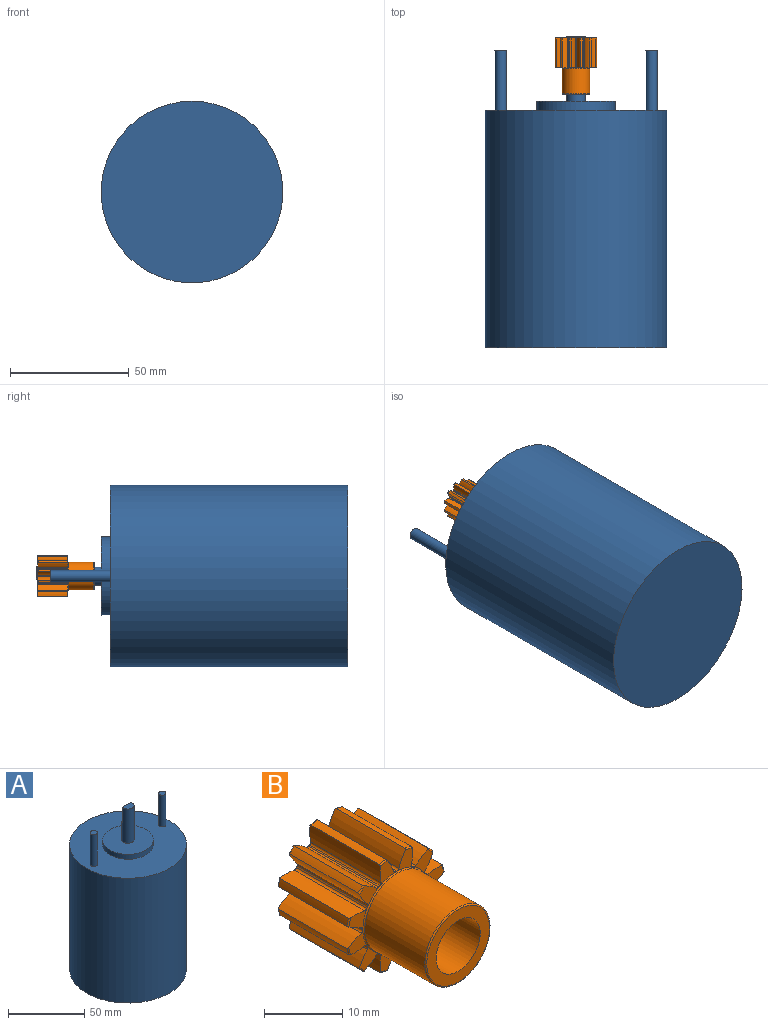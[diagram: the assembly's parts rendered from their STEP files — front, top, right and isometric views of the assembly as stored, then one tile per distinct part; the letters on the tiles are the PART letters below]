
ASSEMBLY  parts=2 mates=1
PART A: 13 faces, bbox 76.5x76.5x131.3 mm
  f0: cylinder r=38.25mm len=100mm, axis (0,0,-1), area 24033.2mm2, adj f1,f2
  f1: plane 76.5x76.5mm, normal (0,0,1), area 3696.7mm2, adj f0,f3,f9,f11
  f2: plane 76.5x76.5mm, normal (0,0,-1), area 4596.3mm2, adj f0
  f3: cylinder r=16.57mm len=33.15mm, axis (0,0,-1), area 402mm2, adj f1,f4
  f4: plane 33.15x33.15mm, normal (0,0,1), area 813.6mm2, adj f3,f5
  f5: cylinder r=3.97mm len=27.45mm, axis (0,0,-1), area 559mm2, adj f4,f6,f7,f8
  f6: plane 7.94x5.24mm, normal (0,0,1), area 34.6mm2, adj f5,f7
  f7: plane 12.7x7.52mm, normal (0,1,0), area 95.5mm2, adj f5,f6,f8
  f8: plane 7.52x2.7mm, normal (0,0,1), area 14.8mm2, adj f5,f7
  f9: cylinder r=2.41mm len=25.4mm, axis (0,0,-1), area 385.1mm2, adj f1,f10
  f10: plane 4.83x4.83mm, normal (0,0,1), area 18.3mm2, adj f9
  f11: cylinder r=2.41mm len=25.4mm, axis (0,0,-1), area 385.1mm2, adj f1,f12
  f12: plane 4.83x4.83mm, normal (0,0,1), area 18.3mm2, adj f11
PART B: 103 faces, bbox 17.5x23.9x17.5 mm
  f0: cylinder r=8.89mm len=12.34mm, axis (0,1,0), area 14.2mm2, adj f1,f2,f94,f98
  f1: torus R=8.71mm, axis (0,-1,0), area 0.3mm2, adj f0,f36,f94,f98
  f2: torus R=8.71mm, axis (0,1,0), area 0.3mm2, adj f0,f38,f94,f98
  f3: cylinder r=8.89mm len=12.34mm, axis (0,1,0), area 14.2mm2, adj f4,f5,f89,f93
  f4: torus R=8.71mm, axis (0,-1,0), area 0.3mm2, adj f3,f36,f89,f93
  f5: torus R=8.71mm, axis (0,1,0), area 0.3mm2, adj f3,f38,f89,f93
  f6: cylinder r=8.89mm len=12.34mm, axis (0,1,0), area 14.2mm2, adj f7,f8,f84,f88
  f7: torus R=8.71mm, axis (0,-1,0), area 0.3mm2, adj f6,f36,f84,f88
  f8: torus R=8.71mm, axis (0,1,0), area 0.3mm2, adj f6,f38,f84,f88
  f9: cylinder r=8.89mm len=12.34mm, axis (0,1,0), area 14.2mm2, adj f10,f11,f79,f83
  f10: torus R=8.71mm, axis (0,-1,0), area 0.3mm2, adj f9,f36,f79,f83
  f11: torus R=8.71mm, axis (0,1,0), area 0.3mm2, adj f9,f38,f79,f83
  f12: cylinder r=8.89mm len=12.34mm, axis (0,1,0), area 14.2mm2, adj f13,f14,f74,f78
  f13: torus R=8.71mm, axis (0,-1,0), area 0.3mm2, adj f12,f36,f74,f78
  f14: torus R=8.71mm, axis (0,1,0), area 0.3mm2, adj f12,f38,f74,f78
  f15: cylinder r=8.89mm len=12.34mm, axis (0,1,0), area 14.2mm2, adj f16,f17,f69,f73
  f16: torus R=8.71mm, axis (0,-1,0), area 0.3mm2, adj f15,f36,f69,f73
  f17: torus R=8.71mm, axis (0,1,0), area 0.3mm2, adj f15,f38,f69,f73
  f18: cylinder r=8.89mm len=12.34mm, axis (0,1,0), area 14.2mm2, adj f19,f20,f64,f68
  f19: torus R=8.71mm, axis (0,-1,0), area 0.3mm2, adj f18,f36,f64,f68
  f20: torus R=8.71mm, axis (0,1,0), area 0.3mm2, adj f18,f38,f64,f68
  f21: cylinder r=8.89mm len=12.34mm, axis (0,1,0), area 14.2mm2, adj f22,f23,f59,f63
  f22: torus R=8.71mm, axis (0,-1,0), area 0.3mm2, adj f21,f36,f59,f63
  f23: torus R=8.71mm, axis (0,1,0), area 0.3mm2, adj f21,f38,f59,f63
  f24: cylinder r=8.89mm len=12.34mm, axis (0,1,0), area 14.2mm2, adj f25,f26,f54,f58
  f25: torus R=8.71mm, axis (0,-1,0), area 0.3mm2, adj f24,f36,f54,f58
  f26: torus R=8.71mm, axis (0,1,0), area 0.3mm2, adj f24,f38,f54,f58
  f27: cylinder r=8.89mm len=12.34mm, axis (0,1,0), area 14.2mm2, adj f28,f29,f49,f53
  f28: torus R=8.71mm, axis (0,-1,0), area 0.3mm2, adj f27,f36,f49,f53
  f29: torus R=8.71mm, axis (0,1,0), area 0.3mm2, adj f27,f38,f49,f53
  f30: cylinder r=8.89mm len=12.34mm, axis (0,1,0), area 14.2mm2, adj f31,f32,f44,f48
  f31: torus R=8.71mm, axis (0,-1,0), area 0.3mm2, adj f30,f36,f44,f48
  f32: torus R=8.71mm, axis (0,1,0), area 0.3mm2, adj f30,f38,f44,f48
  f33: cylinder r=3.97mm len=23.88mm, axis (0,1,0), area 595.4mm2, adj f34,f38
  f34: plane 11.33x11.33mm, normal (0,-1,0), area 51.3mm2, adj f33,f39
  f35: cylinder r=5.84mm len=11.68mm, axis (0,1,0), area 397.2mm2, adj f39,f40
  f36: plane 17.12x17.12mm, normal (0,-1,0), area 65.6mm2, adj f1,f4,f7,f10,f13,f16,f19,f22
  f37: cylinder r=8.89mm len=12.34mm, axis (0,1,0), area 14.2mm2, adj f41,f42,f43,f99
  f38: plane 17.12x17.12mm, normal (0,1,0), area 129.9mm2, adj f2,f5,f8,f11,f14,f17,f20,f23
  f39: torus R=5.66mm, axis (0,-1,0), area 10.1mm2, adj f34,f35
  f40: torus R=6.02mm, axis (0,-1,0), area 10.4mm2, adj f35,f36
  f41: torus R=8.71mm, axis (0,-1,0), area 0.3mm2, adj f36,f37,f43,f99
  f42: torus R=8.71mm, axis (0,1,0), area 0.3mm2, adj f37,f38,f43,f99
  f43: cylinder r=7.62mm len=12.7mm, axis (0,-1,0), area 34.8mm2, adj f36,f37,f38,f41,f42,f47
  f44: cylinder r=7.62mm len=12.7mm, axis (0,-1,0), area 34.8mm2, adj f30,f31,f32,f36,f38,f45
  f45: cylinder r=0.38mm len=12.7mm, axis (0,-1,0), area 6.2mm2, adj f36,f38,f44,f46
  f46: cylinder r=6.03mm len=12.7mm, axis (0,-1,0), area 2.7mm2, adj f36,f38,f45,f47
  f47: cylinder r=0.38mm len=12.7mm, axis (0,-1,0), area 6.2mm2, adj f36,f38,f43,f46
  f48: cylinder r=7.62mm len=12.7mm, axis (0,-1,0), area 34.8mm2, adj f30,f31,f32,f36,f38,f52
  f49: cylinder r=7.62mm len=12.7mm, axis (0,-1,0), area 34.8mm2, adj f27,f28,f29,f36,f38,f50
  f50: cylinder r=0.38mm len=12.7mm, axis (0,-1,0), area 6.2mm2, adj f36,f38,f49,f51
  f51: cylinder r=6.03mm len=12.7mm, axis (0,-1,0), area 2.7mm2, adj f36,f38,f50,f52
  f52: cylinder r=0.38mm len=12.7mm, axis (0,-1,0), area 6.2mm2, adj f36,f38,f48,f51
  f53: cylinder r=7.62mm len=12.7mm, axis (0,-1,0), area 34.8mm2, adj f27,f28,f29,f36,f38,f57
  f54: cylinder r=7.62mm len=12.7mm, axis (0,-1,0), area 34.8mm2, adj f24,f25,f26,f36,f38,f55
  f55: cylinder r=0.38mm len=12.7mm, axis (0,-1,0), area 6.2mm2, adj f36,f38,f54,f56
  f56: cylinder r=6.03mm len=12.7mm, axis (0,-1,0), area 2.7mm2, adj f36,f38,f55,f57
  f57: cylinder r=0.38mm len=12.7mm, axis (0,-1,0), area 6.2mm2, adj f36,f38,f53,f56
  f58: cylinder r=7.62mm len=12.7mm, axis (0,-1,0), area 34.8mm2, adj f24,f25,f26,f36,f38,f62
  f59: cylinder r=7.62mm len=12.7mm, axis (0,-1,0), area 34.8mm2, adj f21,f22,f23,f36,f38,f60
  f60: cylinder r=0.38mm len=12.7mm, axis (0,-1,0), area 6.2mm2, adj f36,f38,f59,f61
  f61: cylinder r=6.03mm len=12.7mm, axis (0,-1,0), area 2.7mm2, adj f36,f38,f60,f62
  f62: cylinder r=0.38mm len=12.7mm, axis (0,-1,0), area 6.2mm2, adj f36,f38,f58,f61
  f63: cylinder r=7.62mm len=12.7mm, axis (0,-1,0), area 34.8mm2, adj f21,f22,f23,f36,f38,f67
  f64: cylinder r=7.62mm len=12.7mm, axis (0,-1,0), area 34.8mm2, adj f18,f19,f20,f36,f38,f65
  f65: cylinder r=0.38mm len=12.7mm, axis (0,-1,0), area 6.2mm2, adj f36,f38,f64,f66
  f66: cylinder r=6.03mm len=12.7mm, axis (0,-1,0), area 2.7mm2, adj f36,f38,f65,f67
  f67: cylinder r=0.38mm len=12.7mm, axis (0,-1,0), area 6.2mm2, adj f36,f38,f63,f66
  f68: cylinder r=7.62mm len=12.7mm, axis (0,-1,0), area 34.8mm2, adj f18,f19,f20,f36,f38,f72
  f69: cylinder r=7.62mm len=12.7mm, axis (0,-1,0), area 34.8mm2, adj f15,f16,f17,f36,f38,f70
  f70: cylinder r=0.38mm len=12.7mm, axis (0,-1,0), area 6.2mm2, adj f36,f38,f69,f71
  f71: cylinder r=6.03mm len=12.7mm, axis (0,-1,0), area 2.7mm2, adj f36,f38,f70,f72
  f72: cylinder r=0.38mm len=12.7mm, axis (0,-1,0), area 6.2mm2, adj f36,f38,f68,f71
  f73: cylinder r=7.62mm len=12.7mm, axis (0,-1,0), area 34.8mm2, adj f15,f16,f17,f36,f38,f77
  f74: cylinder r=7.62mm len=12.7mm, axis (0,-1,0), area 34.8mm2, adj f12,f13,f14,f36,f38,f75
  f75: cylinder r=0.38mm len=12.7mm, axis (0,-1,0), area 6.2mm2, adj f36,f38,f74,f76
  f76: cylinder r=6.03mm len=12.7mm, axis (0,-1,0), area 2.7mm2, adj f36,f38,f75,f77
  f77: cylinder r=0.38mm len=12.7mm, axis (0,-1,0), area 6.2mm2, adj f36,f38,f73,f76
  f78: cylinder r=7.62mm len=12.7mm, axis (0,-1,0), area 34.8mm2, adj f12,f13,f14,f36,f38,f82
  f79: cylinder r=7.62mm len=12.7mm, axis (0,-1,0), area 34.8mm2, adj f9,f10,f11,f36,f38,f80
  f80: cylinder r=0.38mm len=12.7mm, axis (0,-1,0), area 6.2mm2, adj f36,f38,f79,f81
  f81: cylinder r=6.03mm len=12.7mm, axis (0,-1,0), area 2.7mm2, adj f36,f38,f80,f82
  f82: cylinder r=0.38mm len=12.7mm, axis (0,-1,0), area 6.2mm2, adj f36,f38,f78,f81
  f83: cylinder r=7.62mm len=12.7mm, axis (0,-1,0), area 34.8mm2, adj f9,f10,f11,f36,f38,f87
  f84: cylinder r=7.62mm len=12.7mm, axis (0,-1,0), area 34.8mm2, adj f6,f7,f8,f36,f38,f85
  f85: cylinder r=0.38mm len=12.7mm, axis (0,-1,0), area 6.2mm2, adj f36,f38,f84,f86
  f86: cylinder r=6.03mm len=12.7mm, axis (0,-1,0), area 2.7mm2, adj f36,f38,f85,f87
  f87: cylinder r=0.38mm len=12.7mm, axis (0,-1,0), area 6.2mm2, adj f36,f38,f83,f86
  f88: cylinder r=7.62mm len=12.7mm, axis (0,-1,0), area 34.8mm2, adj f6,f7,f8,f36,f38,f92
  f89: cylinder r=7.62mm len=12.7mm, axis (0,-1,0), area 34.8mm2, adj f3,f4,f5,f36,f38,f90
  f90: cylinder r=0.38mm len=12.7mm, axis (0,-1,0), area 6.2mm2, adj f36,f38,f89,f91
  f91: cylinder r=6.03mm len=12.7mm, axis (0,-1,0), area 2.7mm2, adj f36,f38,f90,f92
  f92: cylinder r=0.38mm len=12.7mm, axis (0,-1,0), area 6.2mm2, adj f36,f38,f88,f91
  f93: cylinder r=7.62mm len=12.7mm, axis (0,-1,0), area 34.8mm2, adj f3,f4,f5,f36,f38,f97
  f94: cylinder r=7.62mm len=12.7mm, axis (0,-1,0), area 34.8mm2, adj f0,f1,f2,f36,f38,f95
  f95: cylinder r=0.38mm len=12.7mm, axis (0,-1,0), area 6.2mm2, adj f36,f38,f94,f96
  f96: cylinder r=6.03mm len=12.7mm, axis (0,-1,0), area 2.7mm2, adj f36,f38,f95,f97
  f97: cylinder r=0.38mm len=12.7mm, axis (0,-1,0), area 6.2mm2, adj f36,f38,f93,f96
  f98: cylinder r=7.62mm len=12.7mm, axis (0,-1,0), area 34.8mm2, adj f0,f1,f2,f36,f38,f102
  f99: cylinder r=7.62mm len=12.7mm, axis (0,-1,0), area 34.8mm2, adj f36,f37,f38,f41,f42,f100
  f100: cylinder r=0.38mm len=12.7mm, axis (0,-1,0), area 6.2mm2, adj f36,f38,f99,f101
  f101: cylinder r=6.03mm len=12.7mm, axis (0,-1,0), area 2.7mm2, adj f36,f38,f100,f102
  f102: cylinder r=0.38mm len=12.7mm, axis (0,-1,0), area 6.2mm2, adj f36,f38,f98,f101
PLACE A rot(axis=(-1,0,0),90deg) t=(-119.07,-74.72,89.02)mm
PLACE B t=(-119.07,55.95,89.02)mm
MATE fastened A.f0 <-> B.f2  axis (0,1,0) through (-119.07,56.59,89.02)mm
